# Revit family: Geberit VariForm dikdörtgen lavabo, batarya banklı_PRO_1833255
name_source: partatom
category: Plumbing Fixtures
revit_build: Autodesk Revit 2018 (Build: 20190510_1515(x64)
units: mm (PartAtom-declared; Revit-internal decimal feet)

## family parameters
Always vertical = Yes
Cut with Voids When Loaded = No
OmniClass Number = 23.45.05.21
OmniClass Title = Plumbing Fixtures - Sanitary Disposal Units
Part Type = Normal
Room Calculation Point = Yes
Round Connector Dimension = Use Diameter
Shared = No
Work Plane-Based = No

## types (2) — shared parameters
Application purposes = Tezgah üstü montaj için
Application range = Plumbing fixture
BIM Content Version = GEB MG 1.2
BIM Content revision date = 2020.05.18
Brand = Geberit
CW Connection = Yes
Characteristics = Tüm VariForm banyo mobilyaları için uygundur
Dikdörtgen
Birlikte verilen kesit şablonu sayesinde kolay montaj
Montajı lavabo dolabı ile yapılabilir
Description = Geberit VariForm dikdörtgen lavabo, batarya banklı
GEB_culture = tr-TR
GEB_generic_description = Bathroom collection
GEB_generic_manufacturer = generic
GEB_pimversion = 22.02.12
GEB_processing_type = T
GEB_reference = PRO_1833255
GEB_translations = {"ATT_10673":"EAN code basic data","ATT_10882":"Malzeme","ATT_459792":"Renk / Yüzey","applicationPurposes":"Application purposes","application_range":"Application range","brandName":"Brand","characteristics":"Characteristics","content_creator":"BIM Content creator","content_date_changed":"BIM Content revision date","content_version":"BIM Content Version","key 1000":"Article number key","name":"Name","productBrand":"Product brand","scopeOfDelivery":"Scope of delivery","type":"Type","fixed_material":"Main material"}
HW Connection = No
IfcDescription = Geberit VariForm dikdörtgen lavabo, batarya banklı
IfcExportAs = IfcSanitaryTerminal
IfcExportType = WASHHANDBASIN
LOD300 = No
LOD400 = Yes
Main material = Geberit, Plastic, Opaque white
Malzeme = Seramik
Manufacturer = Geberit
Name = Geberit VariForm dikdörtgen lavabo, batarya banklı
Renk / Yüzey = Beyaz
Scope of delivery = Sabitleme malzemesi
Şablon
Vent Connection = No
Waste Connection = Yes
outlet_flow = 0.0 L/s

## per-type parameters (varying)
| type | 500780_0_view | 500781_0_view | Article number key | EAN code basic data |
| 500.780.01.2 Geberit VariForm dikdörtgen lavabo, batarya banklı | Yes | No | 500.780.01.2 | 4025416690412 |
| 500.781.01.2 Geberit VariForm dikdörtgen lavabo, batarya banklı | No | Yes | 500.781.01.2 | 4025416690535 |

## geometry (parser evidence)
native form markers: Blend x8, Sweep x18
no freeform markers — native parametric forms only
